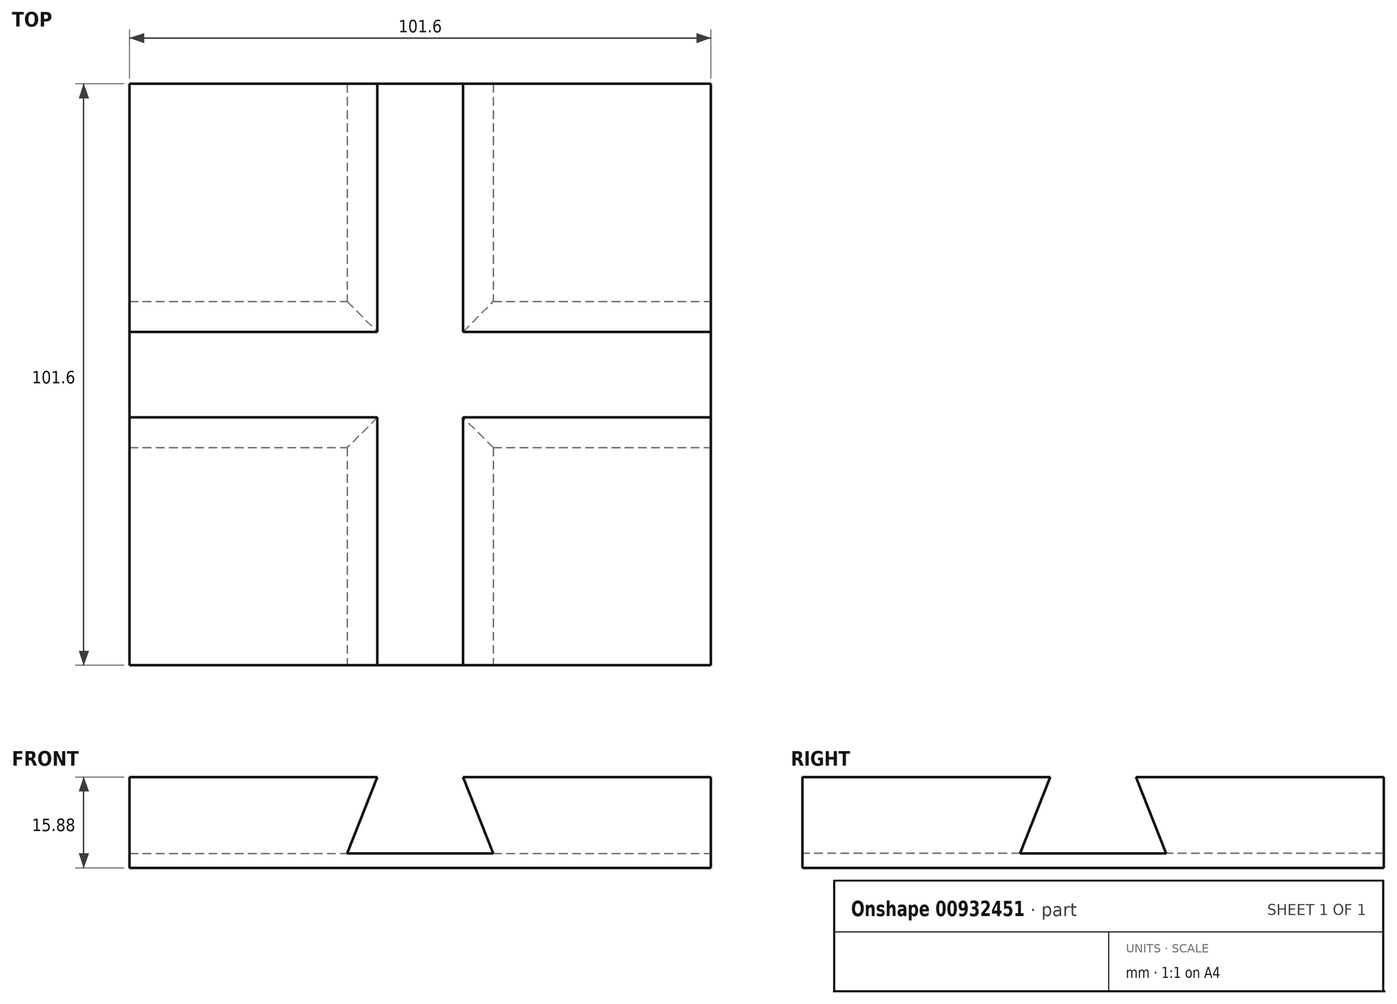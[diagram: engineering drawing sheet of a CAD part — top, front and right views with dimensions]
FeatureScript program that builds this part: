
annotation { "Feature Type Name" : "Feature", "Feature Type Description" : "" }
export const myFeature = defineFeature(function(context is Context, id is Id, definition is map)
    precondition{}
    {
        {
            var Q0;
            Q0=qCreatedBy(makeId("Top.planeOp"),FACE);
            var sketch = newSketch(context, id + "F0", { "sketchPlane" : qUnion([Q0])});
            skLineSegment(sketch, "E0.bottom", {"start": v(50.8, 50.8) * mm, "end": v(-50.8, 50.8) * mm});
            skLineSegment(sketch, "E0.top", {"start": v(50.8, -50.8) * mm, "end": v(-50.8, -50.8) * mm});
            skLineSegment(sketch, "E0.left", {"start": v(50.8, 50.8) * mm, "end": v(50.8, -50.8) * mm});
            skLineSegment(sketch, "E0.right", {"start": v(-50.8, 50.8) * mm, "end": v(-50.8, -50.8) * mm});
            skPoint(sketch, "E0.middle", {"position": v(0, 0) * mm});
            skSolve(sketch);
        }
        {
            var Q0;
            Q0 = qSketchRegion(id + "F0", true);
            extrude(context, id + "F1", {"entities" : qUnion([Q0]), "depth" : 19.05 * mm, "offsetDistance" : 25.4 * mm});
        }
        {
            var Q0;
            Q0=makeQuery(id+"F1.opExtrude","SWEPT_FACE",FACE,{"disambiguationData":[OSD([sQuery(id+"F0.wireOp",EDGE,"E0.left")])]});
            var sketch = newSketch(context, id + "F2", { "sketchPlane" : qUnion([Q0])});
            skLineSegment(sketch, "E1", {"start": v(-6.22, 19.05) * mm, "end": v(-12.76, 2.54) * mm});
            skLineSegment(sketch, "E2", {"start": v(-12.76, 2.54) * mm, "end": v(12.76, 2.54) * mm});
            skLineSegment(sketch, "E3", {"start": v(12.76, 2.54) * mm, "end": v(6.22, 19.05) * mm});
            skLineSegment(sketch, "E4", {"start": v(6.22, 19.05) * mm, "end": v(-6.22, 19.05) * mm});
            skLineSegment(sketch, "E5", {"start": v(0, 19.05) * mm, "end": v(0, 2.54) * mm, "construction": true});
            skSolve(sketch);
        }
        {
            var Q0;
            Q0 = qSketchRegion(id + "F2", true);
            extrude(context, id + "F3", {"entities" : qUnion([Q0]), "operationType" : NewBodyOperationType.REMOVE, "endBound" : BoundingType.THROUGH_ALL, "oppositeDirection" : true, "depth" : 25.4 * mm, "offsetDistance" : 25.4 * mm});
        }
        {
            var Q0;
            Q0=makeQuery(id+"F1.opExtrude","SWEPT_FACE",FACE,{"disambiguationData":[OSD([sQuery(id+"F0.wireOp",EDGE,"E0.top")])]});
            var sketch = newSketch(context, id + "F4", { "sketchPlane" : qUnion([Q0])});
            skLineSegment(sketch, "E6", {"start": v(-6.22, 19.05) * mm, "end": v(-12.76, 2.54) * mm});
            skLineSegment(sketch, "E7", {"start": v(-12.76, 2.54) * mm, "end": v(12.76, 2.54) * mm});
            skLineSegment(sketch, "E8", {"start": v(12.76, 2.54) * mm, "end": v(6.22, 19.05) * mm});
            skLineSegment(sketch, "E9", {"start": v(6.22, 19.05) * mm, "end": v(-6.22, 19.05) * mm});
            skLineSegment(sketch, "E10", {"start": v(0, 19.05) * mm, "end": v(0, 2.54) * mm, "construction": true});
            skSolve(sketch);
        }
        {
            var Q0;
            Q0 = qSketchRegion(id + "F4", true);
            extrude(context, id + "F5", {"entities" : qUnion([Q0]), "operationType" : NewBodyOperationType.REMOVE, "endBound" : BoundingType.THROUGH_ALL, "oppositeDirection" : true, "depth" : 25.4 * mm, "offsetDistance" : 25.4 * mm});
        }
        {
            var Q0;
            Q0=makeQuery(id+"F1.opExtrude","SWEPT_FACE",FACE,{"disambiguationData":[OSD([sQuery(id+"F0.wireOp",EDGE,"E0.left")])]});
            var sketch = newSketch(context, id + "F6", { "sketchPlane" : qUnion([Q0])});
            skLineSegment(sketch, "E11.bottom", {"start": v(-50.8, 19.05) * mm, "end": v(50.8, 19.05) * mm});
            skLineSegment(sketch, "E11.top", {"start": v(-50.8, 15.88) * mm, "end": v(50.8, 15.88) * mm});
            skLineSegment(sketch, "E11.left", {"start": v(-50.8, 19.05) * mm, "end": v(-50.8, 15.88) * mm});
            skLineSegment(sketch, "E11.right", {"start": v(50.8, 19.05) * mm, "end": v(50.8, 15.88) * mm});
            skSolve(sketch);
        }
        {
            var Q0;
            Q0 = qSketchRegion(id + "F6", true);
            extrude(context, id + "F7", {"entities" : qUnion([Q0]), "operationType" : NewBodyOperationType.REMOVE, "endBound" : BoundingType.THROUGH_ALL, "oppositeDirection" : true, "depth" : 25.4 * mm, "offsetDistance" : 25.4 * mm});
        }
    });
